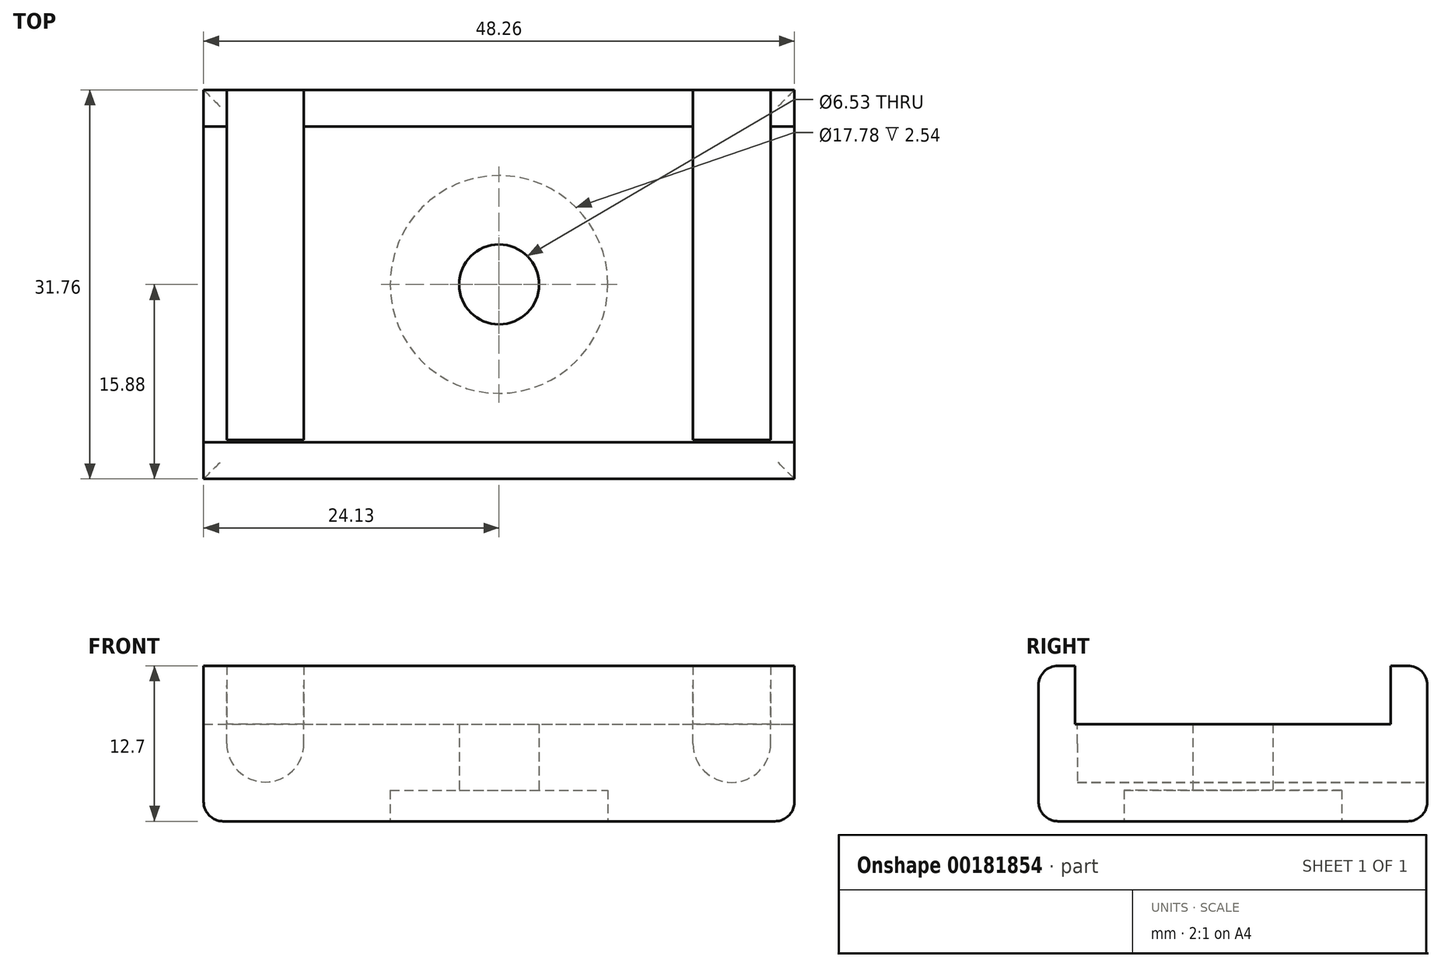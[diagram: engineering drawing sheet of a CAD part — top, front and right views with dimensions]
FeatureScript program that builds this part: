
annotation { "Feature Type Name" : "Feature", "Feature Type Description" : "" }
export const myFeature = defineFeature(function(context is Context, id is Id, definition is map)
    precondition{}
    {
        {
            var Q0;
            Q0=qCreatedBy(makeId("Top.planeOp"),FACE);
            var sketch = newSketch(context, id + "F0", { "sketchPlane" : qUnion([Q0])});
            skLineSegment(sketch, "E0.bottom", {"start": v(24.13, 15.88) * mm, "end": v(-24.13, 15.88) * mm});
            skLineSegment(sketch, "E0.top", {"start": v(24.13, -15.88) * mm, "end": v(-24.13, -15.88) * mm});
            skLineSegment(sketch, "E0.left", {"start": v(24.13, 15.88) * mm, "end": v(24.13, -15.88) * mm});
            skLineSegment(sketch, "E0.right", {"start": v(-24.13, 15.88) * mm, "end": v(-24.13, -15.88) * mm});
            skPoint(sketch, "E0.middle", {"position": v(0, 0) * mm});
            skSolve(sketch);
        }
        {
            var Q0;
            Q0 = qSketchRegion(id + "F0", true);
            extrude(context, id + "F1", {"entities" : qUnion([Q0]), "depth" : 12.7 * mm});
        }
        {
            var Q0;
            Q0=makeQuery(id+"F1.opExtrude","CAP_FACE",FACE,{"disambiguationData":[OSD([sQuery(id+"F0.wireOp",EDGE,"E0.bottom"),sQuery(id+"F0.wireOp",EDGE,"E0.top"),sQuery(id+"F0.wireOp",EDGE,"E0.left"),sQuery(id+"F0.wireOp",EDGE,"E0.right")])],"isStart":false});
            var sketch = newSketch(context, id + "F2", { "sketchPlane" : qUnion([Q0])});
            skLineSegment(sketch, "E1.bottom", {"start": v(-24.13, 12.9) * mm, "end": v(24.13, 12.9) * mm});
            skLineSegment(sketch, "E1.top", {"start": v(-24.13, -12.9) * mm, "end": v(24.13, -12.9) * mm});
            skLineSegment(sketch, "E1.left", {"start": v(-24.13, 12.9) * mm, "end": v(-24.13, -12.9) * mm});
            skLineSegment(sketch, "E1.right", {"start": v(24.13, 12.9) * mm, "end": v(24.13, -12.9) * mm});
            skPoint(sketch, "E1.middle", {"position": v(0, 0) * mm});
            skSolve(sketch);
        }
        {
            var Q0;
            Q0=makeQuery(id+"F2.imprint","IMPRINT",FACE,{"disambiguationData":[TD([[makeQuery(id+"F2.imprint","IMPRINT",EDGE,{"derivedFrom":sQuery(id+"F2.wireOp",EDGE,"E1.bottom")}),-1.0]])]});
            extrude(context, id + "F3", {"entities" : qUnion([Q0]), "operationType" : NewBodyOperationType.REMOVE, "oppositeDirection" : true, "depth" : 4.76 * mm});
        }
        {
            var Q0;
            Q0=makeQuery(id+"F1.opExtrude","SWEPT_FACE",FACE,{"disambiguationData":[OSD([sQuery(id+"F0.wireOp",EDGE,"E0.bottom")])]});
            var sketch = newSketch(context, id + "F4", { "sketchPlane" : qUnion([Q0])});
            skPoint(sketch, "E2.endSnap0", {"position": v(0, 0) * mm});
            skLineSegment(sketch, "E3", {"start": v(-22.19, 6.35) * mm, "end": v(-22.19, 16.05) * mm});
            skLineSegment(sketch, "E4", {"start": v(-15.84, 6.35) * mm, "end": v(-15.84, 16.04) * mm});
            skArc(sketch, "E5", {"start": v(-22.19, 6.35) * mm, "mid": v(-19.01, 3.17) * mm, "end": v(-15.84, 6.35) * mm});
            skLineSegment(sketch, "E6", {"start": v(15.94, 6.35) * mm, "end": v(15.94, 15.78) * mm});
            skLineSegment(sketch, "E7", {"start": v(22.24, 6.35) * mm, "end": v(22.24, 15.77) * mm});
            skArc(sketch, "E8", {"start": v(15.94, 6.35) * mm, "mid": v(19.09, 3.2) * mm, "end": v(22.24, 6.35) * mm});
            skLineSegment(sketch, "E9", {"start": v(-22.19, 16.05) * mm, "end": v(-15.84, 16.04) * mm});
            skLineSegment(sketch, "E10", {"start": v(15.94, 15.78) * mm, "end": v(22.24, 15.77) * mm});
            skSolve(sketch);
        }
        {
            var Q0;
            {var subQ0=sQuery(id+"F4.wireOp",EDGE,"E5");Q0=makeQuery(id+"F4.imprint","IMPRINT",FACE,{"disambiguationData":[TD([[makeQuery(id+"F4.imprint","IMPRINT",EDGE,{"derivedFrom":subQ0}),1.0]])]});}
            var Q1;
            {var subQ0=sQuery(id+"F4.wireOp",EDGE,"E8");Q1=makeQuery(id+"F4.imprint","IMPRINT",FACE,{"disambiguationData":[TD([[makeQuery(id+"F4.imprint","IMPRINT",EDGE,{"derivedFrom":subQ0}),1.0]])]});}
            extrude(context, id + "F5", {"entities" : qUnion([Q0, Q1]), "operationType" : NewBodyOperationType.REMOVE, "oppositeDirection" : true, "depth" : 28.57 * mm});
        }
        {
            var Q0;
            Q0=makeQuery(id+"F1.opExtrude","CAP_FACE",FACE,{"disambiguationData":[OSD([sQuery(id+"F0.wireOp",EDGE,"E0.bottom"),sQuery(id+"F0.wireOp",EDGE,"E0.top"),sQuery(id+"F0.wireOp",EDGE,"E0.left"),sQuery(id+"F0.wireOp",EDGE,"E0.right")])],"isStart":true});
            var sketch = newSketch(context, id + "F6", { "sketchPlane" : qUnion([Q0])});
            skCircle(sketch, "E11", {"center": v(0, 0) * mm, "radius": 3.26 * mm});
            skCircle(sketch, "E12", {"center": v(0, 0) * mm, "radius": 8.9 * mm});
            skSolve(sketch);
        }
        {
            var Q0;
            Q0=makeQuery(id+"F6.imprint","IMPRINT",FACE,{"disambiguationData":[TD([[makeQuery(id+"F6.imprint","IMPRINT",EDGE,{"derivedFrom":sQuery(id+"F6.wireOp",EDGE,"E11")}),1.0]])]});
            extrude(context, id + "F7", {"entities" : qUnion([Q0]), "operationType" : NewBodyOperationType.REMOVE, "endBound" : BoundingType.UP_TO_NEXT, "oppositeDirection" : true, "depth" : 14.22 * mm});
        }
        {
            var Q0;
            Q0=makeQuery(id+"F6.imprint","IMPRINT",FACE,{"disambiguationData":[TD([[makeQuery(id+"F6.imprint","IMPRINT",EDGE,{"derivedFrom":sQuery(id+"F6.wireOp",EDGE,"E11")}),-1.0]])]});
            extrude(context, id + "F8", {"entities" : qUnion([Q0]), "operationType" : NewBodyOperationType.REMOVE, "oppositeDirection" : true, "depth" : 2.54 * mm});
        }
        {
            var Q0;
            Q0=makeQuery(id+"F1.opExtrude","CAP_EDGE",EDGE,{"disambiguationData":[OSD([sQuery(id+"F0.wireOp",EDGE,"E0.left")])],"isStart":true});
            var Q1;
            Q1=makeQuery(id+"F1.opExtrude","CAP_EDGE",EDGE,{"disambiguationData":[OSD([sQuery(id+"F0.wireOp",EDGE,"E0.bottom")])],"isStart":true});
            var Q2;
            Q2=makeQuery(id+"F1.opExtrude","CAP_EDGE",EDGE,{"disambiguationData":[OSD([sQuery(id+"F0.wireOp",EDGE,"E0.right")])],"isStart":true});
            var Q3;
            Q3=makeQuery(id+"F1.opExtrude","CAP_EDGE",EDGE,{"disambiguationData":[OSD([sQuery(id+"F0.wireOp",EDGE,"E0.top")])],"isStart":true});
            var Q4;
            Q4=makeQuery(id+"F8.boolean.opBoolean","COPY",EDGE,{"derivedFrom":makeQuery(id+"F8.opExtrude","CAP_EDGE",EDGE,{"disambiguationData":[OSD([sQuery(id+"F6.wireOp",EDGE,"E12")])],"isStart":true})});
            fillet(context, id + "F9", {"entities" : qUnion([Q0, Q1, Q2, Q3, Q4]), "radius" : 1.59 * mm, "tangentPropagation" : true, "allowEdgeOverflow" : false});
        }
        {
            var Q0;
            {var subQ0=sQuery(id+"F0.wireOp",EDGE,"E0.bottom");Q0=makeQuery(id+"F5.boolean.opBoolean","SPLIT",EDGE,{"disambiguationData":[TD([makeQuery(id+"F5.opExtrude","SWEPT_FACE",FACE,{"disambiguationData":[OSD([sQuery(id+"F4.wireOp",EDGE,"E4")])]})])],"derivedFrom":makeQuery(id+"F1.opExtrude","CAP_EDGE",EDGE,{"disambiguationData":[OSD([subQ0])],"isStart":false})});}
            var Q1;
            Q1=makeQuery(id+"F1.opExtrude","CAP_EDGE",EDGE,{"disambiguationData":[OSD([sQuery(id+"F0.wireOp",EDGE,"E0.top")])],"isStart":false});
            fillet(context, id + "F10", {"entities" : qUnion([Q0, Q1]), "radius" : 1.59 * mm, "tangentPropagation" : true, "allowEdgeOverflow" : false});
        }
        {
            var Q0;
            {var subQ0=sQuery(id+"F0.wireOp",EDGE,"E0.bottom");var subQ1=sQuery(id+"F0.wireOp",EDGE,"E0.right");Q0=makeQuery(id+"F5.boolean.opBoolean","SPLIT",EDGE,{"disambiguationData":[TD([makeQuery(id+"F1.opExtrude","SWEPT_FACE",FACE,{"disambiguationData":[OSD([subQ1])]})])],"derivedFrom":makeQuery(id+"F1.opExtrude","CAP_EDGE",EDGE,{"disambiguationData":[OSD([subQ0])],"isStart":false})});}
            fillet(context, id + "F11", {"entities" : qUnion([Q0]), "radius" : 1.59 * mm, "tangentPropagation" : true, "allowEdgeOverflow" : false});
        }
        {
            var Q0;
            {var subQ0=sQuery(id+"F0.wireOp",EDGE,"E0.bottom");var subQ1=sQuery(id+"F0.wireOp",EDGE,"E0.left");Q0=makeQuery(id+"F5.boolean.opBoolean","SPLIT",EDGE,{"disambiguationData":[TD([makeQuery(id+"F1.opExtrude","SWEPT_FACE",FACE,{"disambiguationData":[OSD([subQ1])]})])],"derivedFrom":makeQuery(id+"F1.opExtrude","CAP_EDGE",EDGE,{"disambiguationData":[OSD([subQ0])],"isStart":false})});}
            fillet(context, id + "F12", {"entities" : qUnion([Q0]), "radius" : 1.59 * mm, "tangentPropagation" : true, "allowEdgeOverflow" : false});
        }
    });
